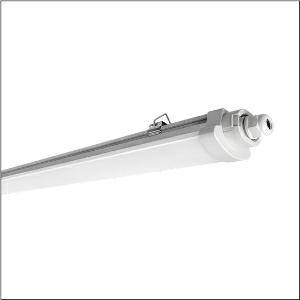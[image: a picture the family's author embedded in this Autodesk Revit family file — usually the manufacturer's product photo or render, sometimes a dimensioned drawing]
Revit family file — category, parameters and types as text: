
# Revit family: monsun_r__41_51fk20mn460a003_94ec
name_source: partatom
category: Lighting Fixtures
units: mm (PartAtom-declared; Revit-internal decimal feet)

## family parameters
Cut with Voids When Loaded = No
Host = Face
Light Source = No
Part Type = Normal
Room Calculation Point = No
Round Connector Dimension = Use Diameter
Shared = No

## types (1)
- --- (1 x LED, 6000 lm, 46 W, 4000K)
    Apparent Load = 46 VA
    CIE Flux Codes = 44 74 91 91 100
    Color Rendering = 80
    Color Temperature = 4000K
    Default Elevation = 1800 mm
    Description = Monsun® 41, damp-proof luminaire, primary optical cover: diffuser, of PC, frosted, light emission: direct distribution, primary light characteristic: symmetric, installation type: suspended mounting, surface-mounted, LED, rated luminous flux: 6.000lm, luminous efficacy: 130lm/W, light colour: 840, colour temperature: 4000K, control gear: ECG Multilumen, with terminal, 3-pole, through-wiring: 3x 1.5mm², mains connection: 220..240V, AC, 50/60Hz, rated input power: 46W, housing, luminaire housing, of PC, grey, length: 1.500mm, width: 79mm, height: 52mm, end cap, of PC, grey, ceiling mounting element, of stainless steel (V2A), protection rating (complete): IP65, insulation class (complete): insulation class II (safety insulation), certification: CE, UKCA, protection symbol: D, impact resistance: IK08, permissible operating ambient temperature: -20..+35°C, corresponds to IFS (International Featured Standards) requirements for safety and quality in the food industry, contact your sales advisor before using the luminaires in applications with unclear chemical exposure, large temperature fluctuations or condensation-forming humidity, packaging unit: 1 piece
    Height = 54 mm
    Lamp = 1 x LED
    Lamp Light Flux = 6000 lm
    Lamp Power = 46 W
    Lamp count = 1
    Length = 1500 mm
    Luminous efficacy = 130 lm/W
    Manufacturer = Siteco
    ModVariant = No
    Model = 51FK20MN460A003
    Mounting Place = Ceiling
    Mounting Type = Surface mounted
    Number of Poles = 1
    OnlyDefault = Yes
    Power Factor = 1
    Product Name = Monsun® 41
    Product group = damp-proof luminaire
    ProductGroupID = 300
    Protection Class = Protection class II
    Protection Degree = IP 65
    RLX_Detail_Level = 1
    RLX_Emergency_Light_Flux = 0 lm
    RLX_Emergency_Type = 0
    RLX_Emergency_Type_DB = No
    RlxData = <blob elided: 28917 chars, md5=be68af25>
    Socket = socket
    Standby Power = 0 W
    System Light Flux = 6000 lm
    System Power = 46 W
    Type Comments = factory setting: luminous flux: 100 % | (HIGH)
    Type Image = l_1007037.jpg
    URL = http://relux.com
    VarID = @adj_145799
    Voltage = 0 V
    Weight = 0.00 kg
    Width = 79 mm

## geometry (parser evidence)
native form markers: Blend x4, Sweep x14
no freeform markers — native parametric forms only
